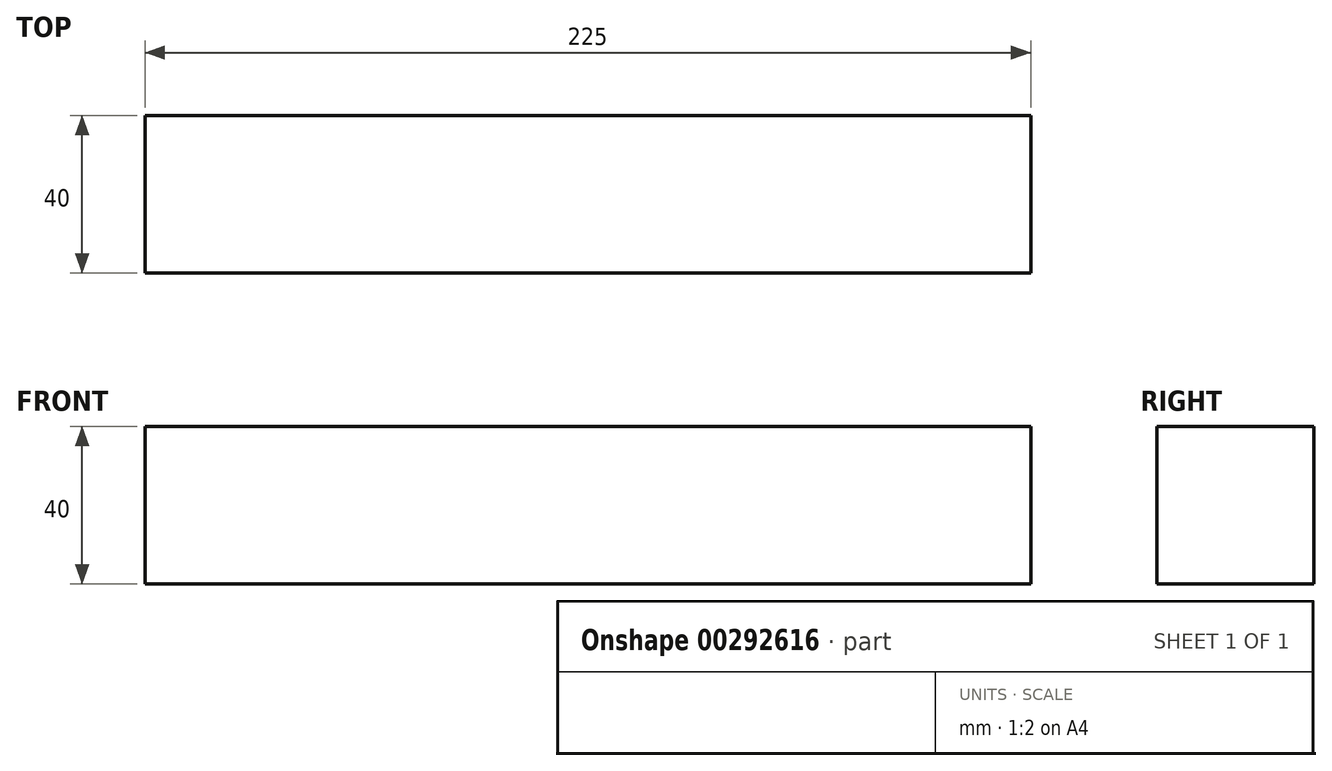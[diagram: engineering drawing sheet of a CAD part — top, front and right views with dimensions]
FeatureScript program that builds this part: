
annotation { "Feature Type Name" : "Feature", "Feature Type Description" : "" }
export const myFeature = defineFeature(function(context is Context, id is Id, definition is map)
    precondition{}
    {
        {
            var Q0;
            Q0=qCreatedBy(makeId("Front.planeOp"),FACE);
            var sketch = newSketch(context, id + "F0", { "sketchPlane" : qUnion([Q0])});
            skLineSegment(sketch, "E0.bottom", {"start": v(0, 40) * mm, "end": v(225, 40) * mm});
            skLineSegment(sketch, "E0.top", {"start": v(0, 0) * mm, "end": v(225, 0) * mm});
            skLineSegment(sketch, "E0.left", {"start": v(0, 40) * mm, "end": v(0, 0) * mm});
            skLineSegment(sketch, "E0.right", {"start": v(225, 40) * mm, "end": v(225, 0) * mm});
            skSolve(sketch);
        }
        {
            var Q0;
            Q0=makeQuery(id+"F0.imprint","IMPRINT",FACE,{"disambiguationData":[TD([[makeQuery(id+"F0.imprint","IMPRINT",EDGE,{"derivedFrom":sQuery(id+"F0.wireOp",EDGE,"E0.bottom")}),-1.0]])]});
            extrude(context, id + "F1", {"entities" : qUnion([Q0]), "depth" : 40 * mm});
        }
    });
